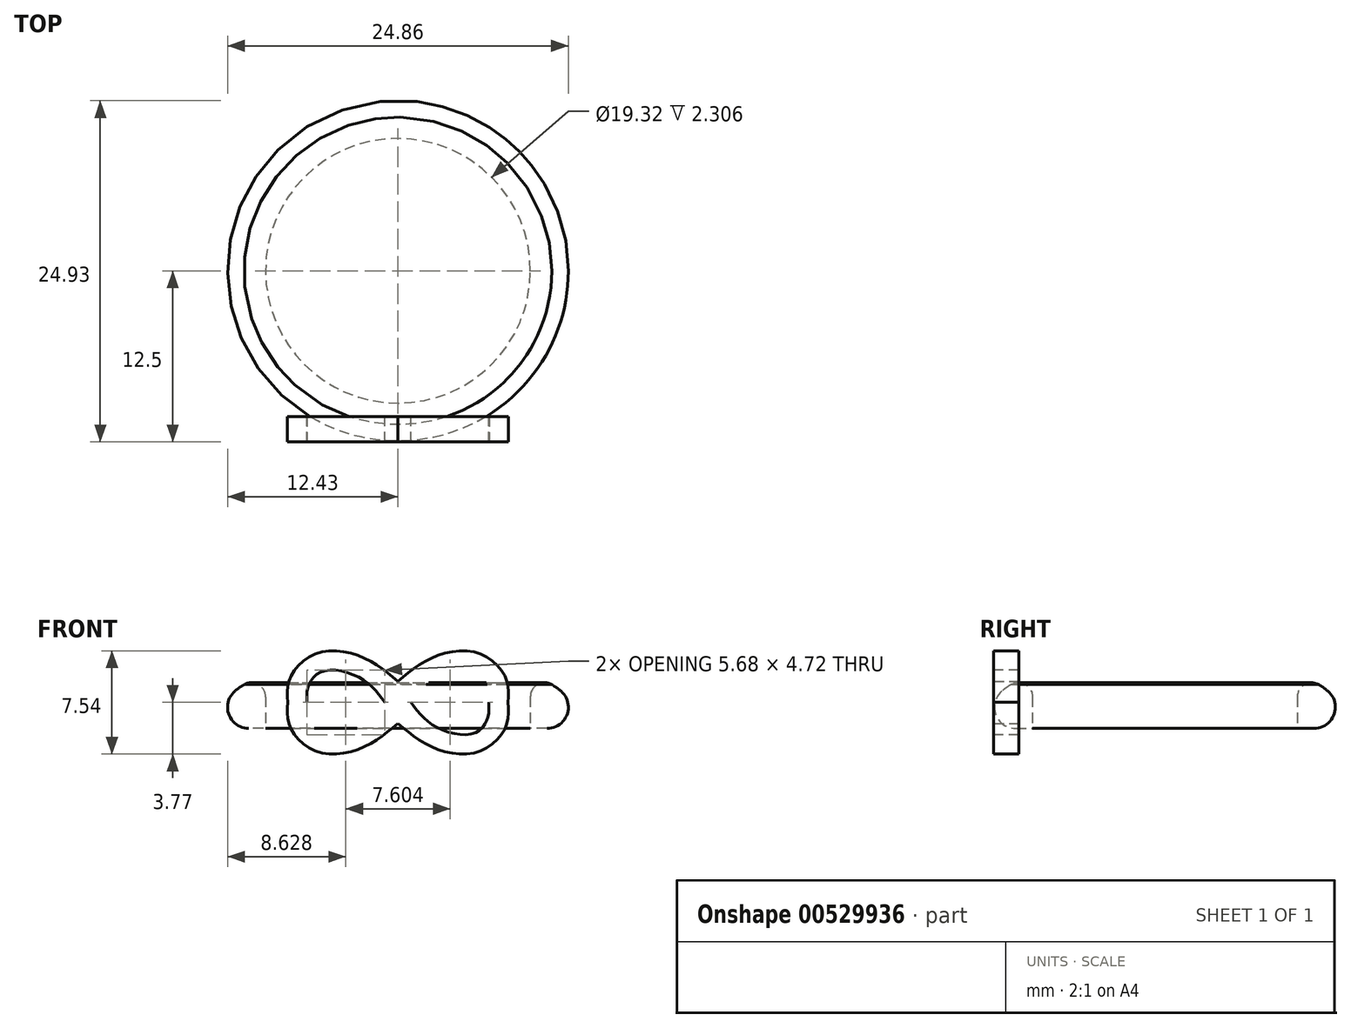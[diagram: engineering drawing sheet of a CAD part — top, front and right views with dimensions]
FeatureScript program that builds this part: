
annotation { "Feature Type Name" : "Feature", "Feature Type Description" : "" }
export const myFeature = defineFeature(function(context is Context, id is Id, definition is map)
    precondition{}
    {
        {
            var Q0;
            Q0=qCreatedBy(makeId("Top.planeOp"),FACE);
            var sketch = newSketch(context, id + "F0", { "sketchPlane" : qUnion([Q0])});
            skCircle(sketch, "E0", {"center": v(0, 0) * mm, "radius": 13.45 * mm});
            skCircle(sketch, "E1", {"center": v(0, 0) * mm, "radius": 9.66 * mm});
            skSolve(sketch);
        }
        {
            var Q0;
            Q0 = qSketchRegion(id + "F0", true);
            extrude(context, id + "F1", {"entities" : qUnion([Q0]), "endBound" : BoundingType.SYMMETRIC, "depth" : 3.8 * mm, "offsetDistance" : 25.4 * mm});
        }
        {
            var Q0;
            Q0=makeQuery(id+"F1.opExtrude","CAP_EDGE",EDGE,{"disambiguationData":[OSD([sQuery(id+"F0.wireOp",EDGE,"E0")])],"isStart":false});
            fillet(context, id + "F2", {"entities" : qUnion([Q0]), "radius" : 5.08 * mm, "tangentPropagation" : true, "rho" : 0.5, "crossSection" : FilletCrossSection.CONIC, "allowEdgeOverflow" : false});
        }
        {
            var Q0;
            {var subQ0=sQuery(id+"F0.wireOp",EDGE,"E0");Q0=makeQuery(id+"F2.opFillet","BLEND_EDGE",EDGE,{"blendedFrom":[makeQuery(id+"F1.opExtrude","CAP_EDGE",EDGE,{"disambiguationData":[OSD([subQ0])],"isStart":false}),makeQuery(id+"F1.opExtrude","CAP_FACE",FACE,{"disambiguationData":[OSD([subQ0,sQuery(id+"F0.wireOp",EDGE,"E1")])],"isStart":true})],"blendedInto":[makeQuery(id+"F1.opExtrude","CAP_FACE",FACE,{"disambiguationData":[OSD([subQ0,sQuery(id+"F0.wireOp",EDGE,"E1")])],"isStart":true})]});}
            fillet(context, id + "F3", {"entities" : qUnion([Q0]), "radius" : 1.55 * mm, "tangentPropagation" : true, "allowEdgeOverflow" : false});
        }
        {
            var Q0;
            Q0=makeQuery(id+"F2.opFillet","BLEND_EDGE",EDGE,{"blendedFrom":[makeQuery(id+"F1.opExtrude","CAP_EDGE",EDGE,{"disambiguationData":[OSD([sQuery(id+"F0.wireOp",EDGE,"E0")])],"isStart":false}),makeQuery(id+"F1.opExtrude","SWEPT_FACE",FACE,{"disambiguationData":[OSD([sQuery(id+"F0.wireOp",EDGE,"E1")])]})],"blendedInto":[makeQuery(id+"F1.opExtrude","SWEPT_FACE",FACE,{"disambiguationData":[OSD([sQuery(id+"F0.wireOp",EDGE,"E1")])]})]});
            fillet(context, id + "F4", {"entities" : qUnion([Q0]), "radius" : 1.04 * mm, "tangentPropagation" : true, "allowEdgeOverflow" : false});
        }
        {
            var Q0;
            Q0=qCreatedBy(makeId("Front.planeOp"),FACE);
            var sketch = newSketch(context, id + "F5", { "sketchPlane" : qUnion([Q0])});
            skFitSpline(sketch, "E2", {"points": [v(0, 7.66) * mm, v(12.34, 16.23) * mm, v(28.73, 18.17) * mm, v(39.16, 9.38) * mm, v(40.2, 0) * mm], "startDerivative": vector(42.95, 36.3) * mm, "endDerivative": vector(-2.61, -45.09) * mm});
            skFitSpline(sketch, "E3", {"points": [v(4.82, 0) * mm, v(13.16, 8.56) * mm, v(27.39, 11.39) * mm, v(32.68, 5.95) * mm, v(33.2, 0) * mm], "startDerivative": vector(24.47, 33.86) * mm, "endDerivative": vector(-1.13, -30.17) * mm});
            skFitSpline(sketch, "E4.MirrorCS", {"points": [v(4.82, 0) * mm, v(13.16, -8.56) * mm, v(27.39, -11.39) * mm, v(32.68, -5.95) * mm, v(33.2, 0) * mm], "startDerivative": vector(24.47, -33.86) * mm, "endDerivative": vector(-1.13, 30.17) * mm});
            skFitSpline(sketch, "E5.MirrorCS", {"points": [v(0, -7.66) * mm, v(12.34, -16.23) * mm, v(28.73, -18.17) * mm, v(39.16, -9.38) * mm, v(40.2, 0) * mm], "startDerivative": vector(42.95, -36.3) * mm, "endDerivative": vector(-2.61, 45.09) * mm});
            skFitSpline(sketch, "E6.MirrorCS", {"points": [v(0, 7.66) * mm, v(-12.34, 16.23) * mm, v(-28.73, 18.17) * mm, v(-39.16, 9.38) * mm, v(-40.2, 0) * mm], "startDerivative": vector(-42.95, 36.3) * mm, "endDerivative": vector(2.61, -45.09) * mm});
            skFitSpline(sketch, "E7.MirrorCS", {"points": [v(-4.82, 0) * mm, v(-13.16, 8.56) * mm, v(-27.39, 11.39) * mm, v(-32.68, 5.95) * mm, v(-33.2, 0) * mm], "startDerivative": vector(-24.47, 33.86) * mm, "endDerivative": vector(1.13, -30.17) * mm});
            skFitSpline(sketch, "E8.MirrorCS", {"points": [v(-4.82, 0) * mm, v(-13.16, -8.56) * mm, v(-27.39, -11.39) * mm, v(-32.68, -5.95) * mm, v(-33.2, 0) * mm], "startDerivative": vector(-24.47, -33.86) * mm, "endDerivative": vector(1.13, 30.17) * mm});
            skFitSpline(sketch, "E9.MirrorCS", {"points": [v(0, -7.66) * mm, v(-12.34, -16.23) * mm, v(-28.73, -18.17) * mm, v(-39.16, -9.38) * mm, v(-40.2, 0) * mm], "startDerivative": vector(-42.95, -36.3) * mm, "endDerivative": vector(2.61, 45.09) * mm});
            skSolve(sketch);
        }
        {
            var Q0;
            Q0=makeQuery(id+"F5.imprint","IMPRINT",FACE,{"disambiguationData":[TD([[makeQuery(id+"F5.imprint","IMPRINT",EDGE,{"derivedFrom":sQuery(id+"F5.wireOp",EDGE,"E2")}),-1.0]])]});
            extrude(context, id + "F6", {"entities" : qUnion([Q0]), "depth" : 2.54 * mm, "offsetDistance" : 25.4 * mm});
        }
        {
            var Q0;
            Q0=makeQuery(id+"F6.opExtrude","SWEPT_BODY",BODY,{"disambiguationData":[OSD([sQuery(id+"F5.wireOp",EDGE,"E2"),sQuery(id+"F5.wireOp",EDGE,"E3"),sQuery(id+"F5.wireOp",EDGE,"E4.MirrorCS"),sQuery(id+"F5.wireOp",EDGE,"E5.MirrorCS"),sQuery(id+"F5.wireOp",EDGE,"E6.MirrorCS"),sQuery(id+"F5.wireOp",EDGE,"E7.MirrorCS"),sQuery(id+"F5.wireOp",EDGE,"E8.MirrorCS"),sQuery(id+"F5.wireOp",EDGE,"E9.MirrorCS")])]});
            transform(context, id + "F7", {"entities" : qUnion([Q0]), "transformType" : TransformType.TRANSLATION_3D, "dx" : 0 * mm, "dy" : -11.68 * mm, "dz" : 0 * mm, "makeCopy" : false});
        }
        {
            var Q0;
            Q0=makeQuery(id+"F6.opExtrude","CAP_FACE",FACE,{"disambiguationData":[OSD([sQuery(id+"F5.wireOp",EDGE,"E2"),sQuery(id+"F5.wireOp",EDGE,"E3"),sQuery(id+"F5.wireOp",EDGE,"E4.MirrorCS"),sQuery(id+"F5.wireOp",EDGE,"E5.MirrorCS"),sQuery(id+"F5.wireOp",EDGE,"E6.MirrorCS"),sQuery(id+"F5.wireOp",EDGE,"E7.MirrorCS"),sQuery(id+"F5.wireOp",EDGE,"E8.MirrorCS"),sQuery(id+"F5.wireOp",EDGE,"E9.MirrorCS")])],"isStart":false});
            var sketch = newSketch(context, id + "F8", { "sketchPlane" : qUnion([Q0])});
            skLineSegment(sketch, "E10", {"start": v(0, 0) * mm, "end": v(0, 7.66) * mm});
            skSolve(sketch);
        }
        {
            var Q0;
            Q0=makeQuery(id+"F6.opExtrude","SWEPT_BODY",BODY,{"disambiguationData":[OSD([sQuery(id+"F5.wireOp",EDGE,"E2"),sQuery(id+"F5.wireOp",EDGE,"E3"),sQuery(id+"F5.wireOp",EDGE,"E4.MirrorCS"),sQuery(id+"F5.wireOp",EDGE,"E5.MirrorCS"),sQuery(id+"F5.wireOp",EDGE,"E6.MirrorCS"),sQuery(id+"F5.wireOp",EDGE,"E7.MirrorCS"),sQuery(id+"F5.wireOp",EDGE,"E8.MirrorCS"),sQuery(id+"F5.wireOp",EDGE,"E9.MirrorCS")])]});
            var Q1;
            Q1=sQuery(id+"F8.wireOp",VERTEX,"E10.start");
            transform(context, id + "F9", {"entities" : qUnion([Q0]), "transformType" : TransformType.SCALE_UNIFORMLY, "scale" : .2, "scalePoint" : qUnion([Q1]), "makeCopy" : false});
        }
        {
            var Q0;
            Q0=makeQuery(id+"F6.opExtrude","CAP_FACE",FACE,{"disambiguationData":[OSD([sQuery(id+"F5.wireOp",EDGE,"E2"),sQuery(id+"F5.wireOp",EDGE,"E3"),sQuery(id+"F5.wireOp",EDGE,"E4.MirrorCS"),sQuery(id+"F5.wireOp",EDGE,"E5.MirrorCS"),sQuery(id+"F5.wireOp",EDGE,"E6.MirrorCS"),sQuery(id+"F5.wireOp",EDGE,"E7.MirrorCS"),sQuery(id+"F5.wireOp",EDGE,"E8.MirrorCS"),sQuery(id+"F5.wireOp",EDGE,"E9.MirrorCS")])],"isStart":false});
            extrude(context, id + "F10", {"entities" : qUnion([Q0]), "operationType" : NewBodyOperationType.ADD, "depth" : 1.35 * mm, "offsetDistance" : 25.4 * mm});
        }
        {
            var Q0;
            Q0=makeQuery(id+"F6.opExtrude","SWEPT_BODY",BODY,{"disambiguationData":[OSD([sQuery(id+"F5.wireOp",EDGE,"E2"),sQuery(id+"F5.wireOp",EDGE,"E3"),sQuery(id+"F5.wireOp",EDGE,"E4.MirrorCS"),sQuery(id+"F5.wireOp",EDGE,"E5.MirrorCS"),sQuery(id+"F5.wireOp",EDGE,"E6.MirrorCS"),sQuery(id+"F5.wireOp",EDGE,"E7.MirrorCS"),sQuery(id+"F5.wireOp",EDGE,"E8.MirrorCS"),sQuery(id+"F5.wireOp",EDGE,"E9.MirrorCS")])]});
            transform(context, id + "F11", {"entities" : qUnion([Q0]), "transformType" : TransformType.TRANSLATION_3D, "dx" : 0 * mm, "dy" : 3.07 * mm, "dz" : 0 * mm, "makeCopy" : false});
        }
    });
